# Revit family: Neri_Lang_PULANL-Pooo
name_source: partatom
category: Apparecchi per illuminazione
revit_build: Autodesk Revit 2018 (Build: 20170927_1515(x64)
units: mm (PartAtom-declared; Revit-internal decimal feet)

## family parameters
Basato su piano di lavoro = No
Condiviso = No
Numero OmniClass = 23.35.47.11
Punto di calcolo locali = No
Quota connettore circolare = Usa diametro
Sempre verticale = Sì
Sorgente d'illuminazione = Sì
Taglio con vuoti quando caricato = No
Tipo di parte = Normale
Titolo OmniClass = Lighting Fixtures

## types (4) — shared parameters
Angolo inclinazione = 90.00°
CRI = >80
Connection = Post top mounting on tubes from Ø 2 1/4" to Ø 3 1/2"
Data Sheet = https://www.nerinorthamerica.com
Design Country = Italy
Diametre = 23"
Driver Function = 1-10V + NCL, NVL + NCL
EPA = 0.135 ft²
Efficacy = 118 Lm/W
Estimated Life = 100.000 h (L90 - Ta 25°C)
Fasteners = Stainless Steel
Filtro dei colori = 16777215
Frequency = 50-60 Hz
Height = 30 1/4"
IES Class = Full Cutoff
IK = 08
IP = 66
Immagine tipo = <Nessuno>
Installation Instructions = https://www.nerinorthamerica.com
Lampada = LED
Luminaire Classification System = BUG: B1 U0 G1
Manufacturer Country = Italy
Manufacturer Name = Neri SpA
MasterFormat 2016 Code = 26 56 00
MasterFormat 2016 Description = Exterior Lighting
Material Main = Cast and Sheet Aluminum
Modello = PNLANL-P
NBS_UniClass2015 Code = Ss_70_80_25_70
NBS_UniClass2015 Description = Roadway Lighting Systems
OmniClass Code = 23-35 47 11
OmniClass Description = Lighting Fixtures
Operative Temperature = -31°F / +122°F
Painting = Standard color Dark Grey, type Neri
Painting Steps = Information about paint steps used in this product in specific technical sheet
Product Certification = UL Standard 1598 (C, US)
Product Name = Lang - LED P
Produttore = Neri SpA
Screen = Prismatic, opal white or clear tempered glass
URL = https://www.nerinorthamerica.com
UniFormat II Code = D5020
UniFormat II Description = Lighting and Branch Wiring
Variazione temperatura colore lampada con luminosità attenuata = <Nessuno>
Voltage = 120-277 V
W = 38
Weight = 37.4 lb

## per-type parameters (varying)
| type | File diagramma fotometrico | Lighting Distribution |
| PULANL_Type II | Neri NA Lang Type II 4000K 4500lm prismatic.IES | Type II |
| PULANL_Type III | Neri NA Lang Type III 4000K 4500lm prismatic.IES | Type III |
| PULANL_Type IV | Neri NA Lang Type IV 4000K 4500lm prismatic.IES | Type IV |
| PULANL_Type V | Neri NA Lang Type V 4000K 4500lm prismatic.IES | Type V |
